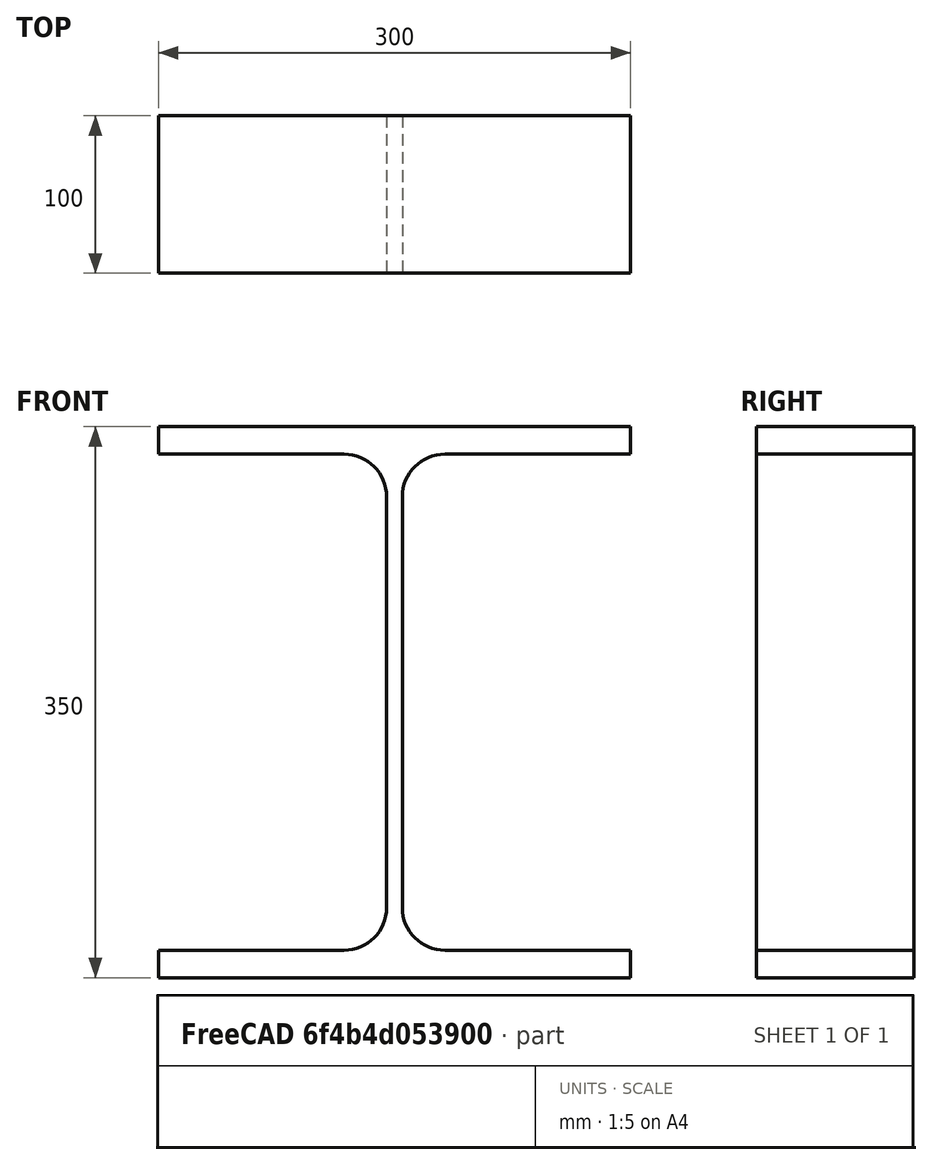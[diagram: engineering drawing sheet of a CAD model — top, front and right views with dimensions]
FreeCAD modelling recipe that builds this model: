
FCSTD DOCUMENT  (FreeCAD 0.21R33694 (Git))
Label: Profile HEA
License: All rights reserved
LicenseURL: http://en.wikipedia.org/wiki/All_rights_reserved
objects: Sketcher::SketchObject×1, Spreadsheet::Sheet×1, PartDesign::Pad×1, PartDesign::Body×1
note: 4 computed .brp shape members not serialized (recipe doc carries the construction recipe); baked Part::Feature solids carry a one-line shape summary decoded from their .brp

FEATURE [Sketcher::SketchObject] Sketch  label="Sk_HEA"
  AttacherType = A
  FullyConstrained = true
  Placement = pos=(0,0,0) rot=(1,0,0;1.5708rad)
  expr: .Constraints.bb = Spreadsheet.HEA_b
  expr: .Constraints.e1 = Spreadsheet.HEA_e1
  expr: .Constraints.ee = Spreadsheet.HEA_e
  expr: .Constraints.hh = Spreadsheet.HEA_h
  expr: .Constraints.rr = Spreadsheet.HEA_r
  sketch-geometry (16):
    g0: ArcOfCircle CenterX=-32 CenterY=-130.5 CenterZ=0 NormalX=0 NormalY=0 NormalZ=1 AngleXU=0 Radius=27 StartAngle=4.71239 EndAngle=6.28319
    g1: ArcOfCircle CenterX=32 CenterY=-130.5 CenterZ=0 NormalX=0 NormalY=0 NormalZ=1 AngleXU=0 Radius=27 StartAngle=3.14159 EndAngle=4.71239
    g2: ArcOfCircle CenterX=32 CenterY=130.5 CenterZ=0 NormalX=0 NormalY=0 NormalZ=1 AngleXU=0 Radius=27 StartAngle=1.5708 EndAngle=3.14159
    g3: ArcOfCircle CenterX=-32 CenterY=130.5 CenterZ=0 NormalX=0 NormalY=0 NormalZ=1 AngleXU=0 Radius=27 StartAngle=2e-16 EndAngle=1.5708
    g4: LineSegment StartX=-150 StartY=-175 StartZ=0 EndX=150 EndY=-175 EndZ=0
    g5: LineSegment StartX=150 StartY=-175 StartZ=0 EndX=150 EndY=-157.5 EndZ=0
    g6: LineSegment StartX=-150 StartY=-175 StartZ=0 EndX=-150 EndY=-157.5 EndZ=0
    g7: LineSegment StartX=-150 StartY=-157.5 StartZ=0 EndX=-32 EndY=-157.5 EndZ=0
    g8: LineSegment StartX=150 StartY=-157.5 StartZ=0 EndX=32 EndY=-157.5 EndZ=0
    g9: LineSegment StartX=5 StartY=-130.5 StartZ=0 EndX=5 EndY=130.5 EndZ=0
    g10: LineSegment StartX=32 StartY=157.5 StartZ=0 EndX=150 EndY=157.5 EndZ=0
    g11: LineSegment StartX=150 StartY=157.5 StartZ=0 EndX=150 EndY=175 EndZ=0
    g12: LineSegment StartX=-150 StartY=157.5 StartZ=0 EndX=-32 EndY=157.5 EndZ=0
    g13: LineSegment StartX=-5 StartY=130.5 StartZ=0 EndX=-5 EndY=-130.5 EndZ=0
    g14: LineSegment StartX=-150 StartY=157.5 StartZ=0 EndX=-150 EndY=175 EndZ=0
    g15: LineSegment StartX=150 StartY=175 StartZ=0 EndX=-150 EndY=175 EndZ=0
  constraints (40):
    c: DistanceX(g4,g4) = 300  'bb'
    c: Radius(g0) = 27  'rr'
    c: DistanceX(g0,g1) = 10  'ee'
    c: DistanceY(g4,g11) = 350  'hh'
    c: DistanceY(g6,g6) = 17.5  'e1'
    c: Coincident(g10,g11)
    c: Coincident(g5,g8)
    c: Coincident(g4,g5)
    c: Coincident(g4,g6)
    c: Coincident(g6,g7)
    c: Symmetric(g6,g5,g-2)
    c: Symmetric(g12,g10,g-2)
    c: Horizontal(g4)
    c: Horizontal(g7)
    c: Equal(g7,g8)
    c: Equal(g8,g10)
    c: Equal(g10,g12)
    c: Tangent(g0,g7) = -1.5708
    c: Tangent(g0,g13) = 1.5708
    c: Tangent(g3,g13) = 1.5708
    c: Tangent(g3,g12) = 1.5708
    c: Tangent(g2,g10) = 1.5708
    c: Tangent(g2,g9) = 1.5708
    c: Tangent(g1,g9) = 1.5708
    c: Tangent(g1,g8) = 1.5708
    c: Equal(g6,g5)
    c: Equal(g5,g11)
    c: Vertical(g6)
    c: Vertical(g11)
    c: Horizontal(g12)
    c: Horizontal(g10)
    c: Horizontal(g8)
    c: Symmetric(g0,g1,g-2)
    c: Symmetric(g2,g1,g-1)
    c: Equal(g1,g2)
    c: Coincident(g14,g12)
    c: Vertical(g14)
    c: Coincident(g15,g11)
    c: Coincident(g15,g14)
    c: Horizontal(g15)
FEATURE [Spreadsheet::Sheet] Spreadsheet  label="Sp_HEA"
  cells = A1==hiddenref(Body.Configuration.String); B1(HEA_h)==.B15; C1(HEA_b)==.C15; D1(HEA_e)==.D15; E1(HEA_e1)==.E15; F1(HEA_r)==.F15; G1(HEA_Label)==.G15; A2(HEA_100)='HEA 100; B2=96; C2=100; D2=5; E2=8; F2=12; G2='HEA 100; A3(HEA_120)='HEA 120; B3=114; C3=120; D3=5; E3=8; F3=12; G3='HEA 120; A4(HEA_140)='HEA 140; B4=133; C4=140; D4=5.5; E4=8.5; F4=12; G4='HEA 140; A5(HEA_160)='HEA 160; B5=152; C5=160; D5=6; E5=9; F5=15; G5='HEA 160; A6(HEA_180)='HEA 180; B6=171; C6=180; D6=6; E6=9.5; F6=15; G6='HEA 180; A7(HEA_200)='HEA 200; B7=190; C7=200; D7=6.5; E7=10; F7=18; G7='HEA 200; A8(HEA_220)='HEA 220; B8=210; C8=220; D8=7; E8=11; F8=21; G8='HEA 220; A9(HEA_240)='HEA 240; B9=230; C9=240; D9=7.5; E9=12; F9=24; G9='HEA 240; A10(HEA_260)='HEA 260; B10=250; C10=260; D10=7.5; E10=12.5; F10=24; G10='HEA 260; A11(HEA_280)='HEA 280; B11=270; C11=280; D11=8; E11=13; F11=27; G11='HEA 280; A12(HEA_300)='HEA 300; B12=290; C12=300; D12=8.5; E12=14; F12=27; G12='HEA 300; A13='HEA 320; B13=310; C13=300; D13=9; E13=15.5; F13=27; G13='HEA 320; A14='HEA 340; B14=330; C14=300; D14=9.5; E14=16.5; F14=27; G14='HEA 340; A15='HEA 360; B15=350; C15=300; D15=10; E15=17.5; F15=27; G15='HEA 360; A16='HEA 400; B16=390; C16=300; D16=11; E16=19; F16=27; G16='HEA 400; A17='HEA 450; B17=440; C17=300; D17=11.5; E17=21; F17=27; G17='HEA 450; A18='HEA 500; B18=490; C18=300; D18=12; E18=23; F18=27; G18='HEA 500; A19='HEA 550; B19=540; C19=300; D19=12.5; E19=24; F19=27; G19='HEA 550; A20='HEA 600; B20=590; C20=300; D20=13; E20=25; F20=27; G20='HEA 600; A21='HEA 650; B21=640; C21=300; D21=13.5; E21=26; F21=27; G21='HEA 650; A22='HEA 700; B22=690; C22=300; D22=14.5; E22=27; F22=27; G22='HEA 700; A23='HEA 800; B23=790; C23=300; D23=15; E23=28; F23=30; G23='HEA 800; A24='HEA 900; B24=890; C24=300; D24=16; E24=30; F24=30; G24='HEA 900; A25='HEA 1000; B25=990; C25=300; D25=16.5; E25=31; F25=30; G25='HEA 1000
  expr: .cells.Bind.B1.ZZ1 = tuple(.cells; <<B>> + str(hiddenref(Body.Configuration) + 2); <<ZZ>> + str(hiddenref(Body.Configuration) + 2))
FEATURE [PartDesign::Pad] Pad
  Direction = (0,-1,2e-16)
  Length = 100
  Length2 = 10
  Placement = pos=(0,0,0) rot=(1,0,0;1.5708rad)
  Profile = -> Sketch
  ReferenceAxis = -> Sketch [N_Axis]
  Type = 0
FEATURE [PartDesign::Body] Body  label="HEA 360"
  Configuration = 13
  Group = -> [Sketch,Pad]
  Origin = -> Origin
  Tip = -> Pad
  expr: .Configuration.Enum = Spreadsheet.cells[<<A2:|>>]
  expr: Label = Spreadsheet.HEA_Label
